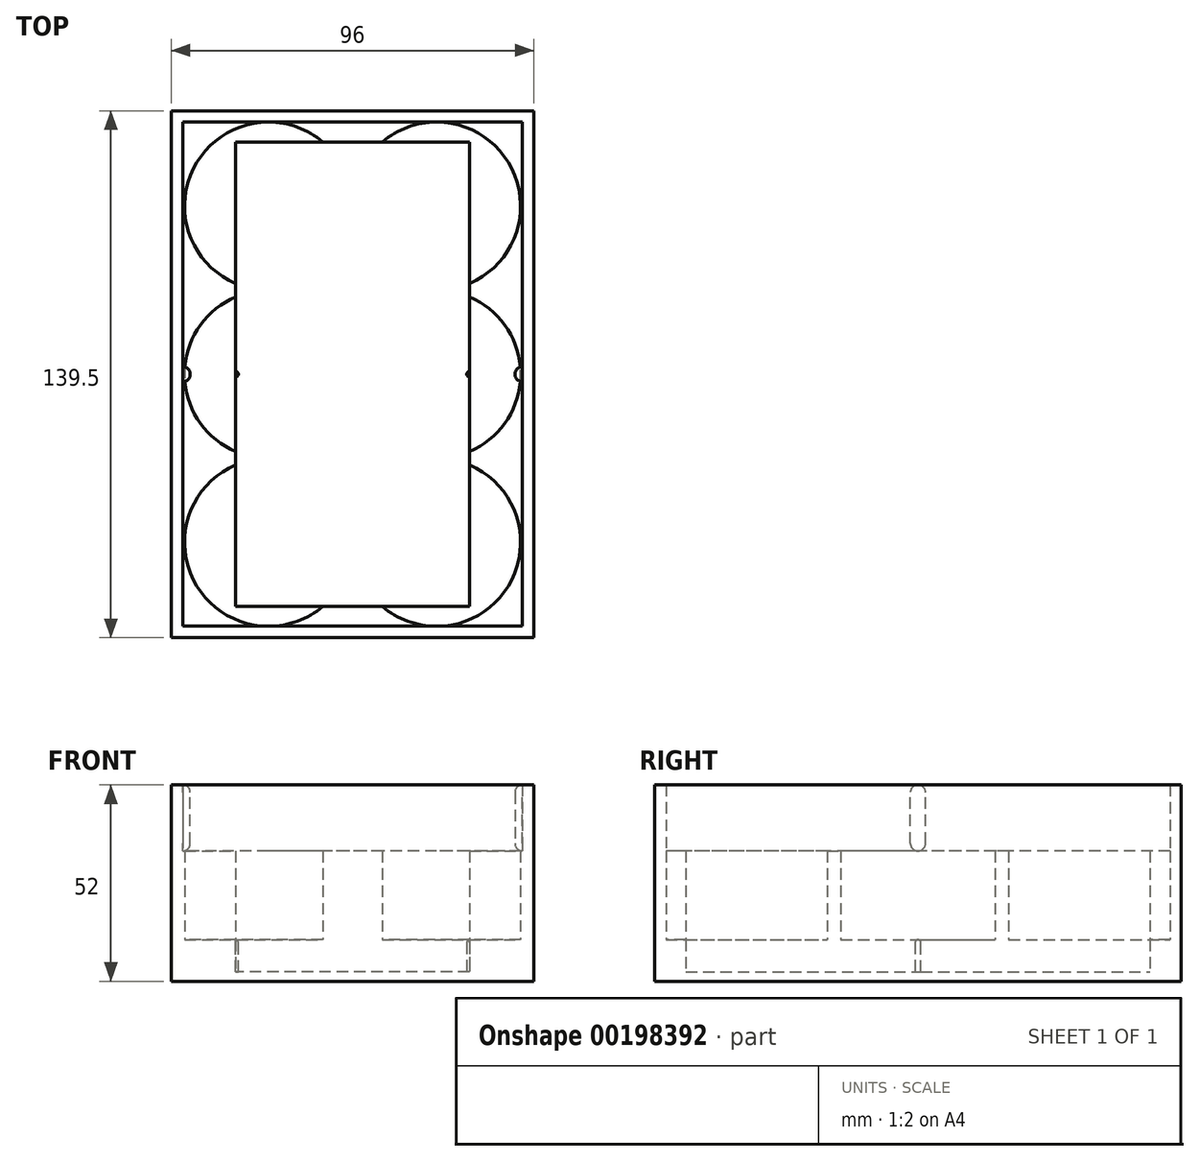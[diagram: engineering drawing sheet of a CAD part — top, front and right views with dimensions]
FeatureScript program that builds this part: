
annotation { "Feature Type Name" : "Feature", "Feature Type Description" : "" }
export const myFeature = defineFeature(function(context is Context, id is Id, definition is map)
    precondition{}
    {
        {
            var Q0;
            Q0=qCreatedBy(makeId("Top.planeOp"),FACE);
            var sketch = newSketch(context, id + "F0", { "sketchPlane" : qUnion([Q0])});
            skLineSegment(sketch, "E0.rect.bottom", {"start": v(47, 68.75) * mm, "end": v(-47, 68.75) * mm});
            skLineSegment(sketch, "E0.rect.top", {"start": v(47, -68.75) * mm, "end": v(-47, -68.75) * mm});
            skLineSegment(sketch, "E0.rect.left", {"start": v(47, 68.75) * mm, "end": v(47, -68.75) * mm});
            skLineSegment(sketch, "E0.rect.right", {"start": v(-47, 68.75) * mm, "end": v(-47, -68.75) * mm});
            skPoint(sketch, "E0.rect.middle", {"position": v(0, 0) * mm});
            skSolve(sketch);
        }
        {
            var Q0;
            Q0=qSketchRegion(id+"F0",true);
            extrude(context, id + "F1", {"entities" : qUnion([Q0]), "depth" : 2.5 * mm});
        }
        {
            var Q0;
            Q0=makeQuery(id+"F1.opExtrude","CAP_FACE",FACE,{"disambiguationData":[OSD([sQuery(id+"F0.wireOp",EDGE,"E0.rect.bottom"),sQuery(id+"F0.wireOp",EDGE,"E0.rect.top"),sQuery(id+"F0.wireOp",EDGE,"E0.rect.left"),sQuery(id+"F0.wireOp",EDGE,"E0.rect.right")])],"isStart":false});
            var sketch = newSketch(context, id + "F2", { "sketchPlane" : qUnion([Q0])});
            skLineSegment(sketch, "E1.rect.bottom", {"start": v(47, 68.75) * mm, "end": v(-47, 68.75) * mm});
            skLineSegment(sketch, "E1.rect.top", {"start": v(47, -68.75) * mm, "end": v(-47, -68.75) * mm});
            skLineSegment(sketch, "E1.rect.left", {"start": v(47, 68.75) * mm, "end": v(47, -68.75) * mm});
            skLineSegment(sketch, "E1.rect.right", {"start": v(-47, 68.75) * mm, "end": v(-47, -68.75) * mm});
            skPoint(sketch, "E1.rect.middle", {"position": v(0, 0) * mm});
            skLineSegment(sketch, "E2.rect.bottom", {"start": v(31, -61.5) * mm, "end": v(-31, -61.5) * mm});
            skLineSegment(sketch, "E2.rect.top", {"start": v(31, 61.5) * mm, "end": v(-31, 61.5) * mm});
            skLineSegment(sketch, "E2.rect.left", {"start": v(31, -61.5) * mm, "end": v(31, 61.5) * mm});
            skLineSegment(sketch, "E2.rect.right", {"start": v(-31, -61.5) * mm, "end": v(-31, 61.5) * mm});
            skSolve(sketch);
        }
        {
            var Q0;
            Q0=qSketchRegion(id+"F2",true);
            extrude(context, id + "F3", {"entities" : qUnion([Q0]), "operationType" : NewBodyOperationType.ADD, "depth" : 8.5 * mm});
        }
        {
            var Q0;
            Q0=makeQuery(id+"F3.opExtrude","CAP_FACE",FACE,{"disambiguationData":[OSD([sQuery(id+"F2.wireOp",EDGE,"E1.rect.bottom"),sQuery(id+"F2.wireOp",EDGE,"E1.rect.top"),sQuery(id+"F2.wireOp",EDGE,"E1.rect.left"),sQuery(id+"F2.wireOp",EDGE,"E1.rect.right"),sQuery(id+"F2.wireOp",EDGE,"E2.rect.bottom"),sQuery(id+"F2.wireOp",EDGE,"E2.rect.top"),sQuery(id+"F2.wireOp",EDGE,"E2.rect.left"),sQuery(id+"F2.wireOp",EDGE,"E2.rect.right")])],"isStart":false});
            var sketch = newSketch(context, id + "F4", { "sketchPlane" : qUnion([Q0])});
            skPoint(sketch, "E3.rect.middle", {"position": v(0, 0) * mm});
            skCircle(sketch, "E4", {"center": v(-22.25, 44.5) * mm, "radius": 22.25 * mm});
            skCircle(sketch, "E5", {"center": v(-22.25, -44.5) * mm, "radius": 22.25 * mm});
            skCircle(sketch, "E6", {"center": v(22.25, -44.5) * mm, "radius": 22.25 * mm});
            skCircle(sketch, "E7", {"center": v(22.25, 0) * mm, "radius": 22.25 * mm});
            skCircle(sketch, "E8", {"center": v(-22.25, 0) * mm, "radius": 22.25 * mm});
            skCircle(sketch, "E9", {"center": v(22.25, 44.5) * mm, "radius": 22.25 * mm});
            skLineSegment(sketch, "E10.rect.bottom", {"start": v(47, -68.75) * mm, "end": v(-47, -68.75) * mm});
            skLineSegment(sketch, "E10.rect.top", {"start": v(47, 68.75) * mm, "end": v(-47, 68.75) * mm});
            skLineSegment(sketch, "E10.rect.left", {"start": v(47, -68.75) * mm, "end": v(47, 68.75) * mm});
            skLineSegment(sketch, "E10.rect.right", {"start": v(-47, -68.75) * mm, "end": v(-47, 68.75) * mm});
            skLineSegment(sketch, "E11", {"start": v(-22.25, 44.5) * mm, "end": v(22.25, 44.5) * mm});
            skLineSegment(sketch, "E12", {"start": v(-22.25, 0) * mm, "end": v(22.25, 0) * mm});
            skLineSegment(sketch, "E13", {"start": v(-22.25, -44.5) * mm, "end": v(22.25, -44.5) * mm});
            skSolve(sketch);
        }
        {
            var Q0;
            Q0=qSketchRegion(id+"F4",true);
            extrude(context, id + "F5", {"entities" : qUnion([Q0]), "operationType" : NewBodyOperationType.ADD, "depth" : 23.5 * mm});
        }
        {
            var Q0;
            {var subQ0=sQuery(id+"F2.wireOp",EDGE,"E2.rect.top");var subQ1=sQuery(id+"F2.wireOp",EDGE,"E2.rect.right");var subQ2=sQuery(id+"F4.wireOp",EDGE,"E4");Q0=makeQuery(id+"F5.boolean.opBoolean","SPLIT",FACE,{"disambiguationData":[TD([makeQuery(id+"F5.opExtrude","SWEPT_FACE",FACE,{"disambiguationData":[OSD([subQ2])]})])],"derivedFrom":makeQuery(id+"F3.opExtrude","CAP_FACE",FACE,{"disambiguationData":[OSD([sQuery(id+"F2.wireOp",EDGE,"E1.rect.bottom"),sQuery(id+"F2.wireOp",EDGE,"E1.rect.top"),sQuery(id+"F2.wireOp",EDGE,"E1.rect.left"),sQuery(id+"F2.wireOp",EDGE,"E1.rect.right"),sQuery(id+"F2.wireOp",EDGE,"E2.rect.bottom"),subQ0,sQuery(id+"F2.wireOp",EDGE,"E2.rect.left"),subQ1])],"isStart":false})});}
            var sketch = newSketch(context, id + "F6", { "sketchPlane" : qUnion([Q0])});
            skLineSegment(sketch, "E14.rect.bottom", {"start": v(-31, 61.5) * mm, "end": v(31, 61.5) * mm});
            skLineSegment(sketch, "E14.rect.top", {"start": v(-31, -61.5) * mm, "end": v(31, -61.5) * mm});
            skLineSegment(sketch, "E14.rect.left", {"start": v(-31, 61.5) * mm, "end": v(-31, -61.5) * mm});
            skLineSegment(sketch, "E14.rect.right", {"start": v(31, 61.5) * mm, "end": v(31, -61.5) * mm});
            skPoint(sketch, "E14.rect.middle", {"position": v(0, 0) * mm});
            skSolve(sketch);
        }
        {
            var Q0;
            Q0=qSketchRegion(id+"F6",true);
            extrude(context, id + "F7", {"entities" : qUnion([Q0]), "operationType" : NewBodyOperationType.REMOVE, "endBound" : BoundingType.THROUGH_ALL, "depth" : 25 * mm});
        }
        {
            var Q0;
            Q0=makeQuery(id+"F5.opExtrude","CAP_FACE",FACE,{"disambiguationData":[OSD([sQuery(id+"F4.wireOp",EDGE,"E4"),sQuery(id+"F4.wireOp",EDGE,"E5"),sQuery(id+"F4.wireOp",EDGE,"E6"),sQuery(id+"F4.wireOp",EDGE,"E7"),sQuery(id+"F4.wireOp",EDGE,"E8"),sQuery(id+"F4.wireOp",EDGE,"E9"),sQuery(id+"F4.wireOp",EDGE,"E10.rect.bottom"),sQuery(id+"F4.wireOp",EDGE,"E10.rect.top"),sQuery(id+"F4.wireOp",EDGE,"E10.rect.left"),sQuery(id+"F4.wireOp",EDGE,"E10.rect.right")])],"isStart":false});
            var sketch = newSketch(context, id + "F8", { "sketchPlane" : qUnion([Q0])});
            skLineSegment(sketch, "E15.rect.bottom", {"start": v(47, 68.75) * mm, "end": v(-47, 68.75) * mm});
            skLineSegment(sketch, "E15.rect.top", {"start": v(47, -68.75) * mm, "end": v(-47, -68.75) * mm});
            skLineSegment(sketch, "E15.rect.left", {"start": v(47, 68.75) * mm, "end": v(47, -68.75) * mm});
            skLineSegment(sketch, "E15.rect.right", {"start": v(-47, 68.75) * mm, "end": v(-47, -68.75) * mm});
            skPoint(sketch, "E15.rect.middle", {"position": v(0, 0) * mm});
            skLineSegment(sketch, "E16.rect.bottom", {"start": v(45, 66.75) * mm, "end": v(-45, 66.75) * mm});
            skLineSegment(sketch, "E16.rect.top", {"start": v(45, -66.75) * mm, "end": v(-45, -66.75) * mm});
            skLineSegment(sketch, "E16.rect.left", {"start": v(45, 66.75) * mm, "end": v(45, -66.75) * mm});
            skLineSegment(sketch, "E16.rect.right", {"start": v(-45, 66.75) * mm, "end": v(-45, -66.75) * mm});
            skSolve(sketch);
        }
        {
            var Q0;
            Q0=qSketchRegion(id+"F8",true);
            extrude(context, id + "F9", {"entities" : qUnion([Q0]), "operationType" : NewBodyOperationType.ADD, "depth" : 17.5 * mm});
        }
        {
            var Q0;
            Q0=makeQuery(id+"F9.opExtrude","SWEPT_FACE",FACE,{"disambiguationData":[OSD([sQuery(id+"F8.wireOp",EDGE,"E16.rect.right")])]});
            var sketch = newSketch(context, id + "F10", { "sketchPlane" : qUnion([Q0])});
            skLineSegment(sketch, "E17", {"start": v(0, 34.5) * mm, "end": v(0, 52) * mm});
            skLineSegment(sketch, "E18", {"start": v(0, 52) * mm, "end": v(0, 50) * mm});
            skLineSegment(sketch, "E19", {"start": v(0, 34.5) * mm, "end": v(0, 36.5) * mm});
            skLineSegment(sketch, "E20", {"start": v(2, 50) * mm, "end": v(2, 36.5) * mm});
            skLineSegment(sketch, "E21", {"start": v(0, 52) * mm, "end": v(0, 34.5) * mm});
            skArc(sketch, "E22", {"start": v(2, 50) * mm, "mid": v(1.41, 51.41) * mm, "end": v(0, 52) * mm});
            skArc(sketch, "E23", {"start": v(0, 34.5) * mm, "mid": v(1.41, 35.09) * mm, "end": v(2, 36.5) * mm});
            skSolve(sketch);
        }
        {
            var Q0;
            Q0=qSketchRegion(id+"F10",true);
            var Q1;
            Q1=sQuery(id+"F10.wireOp",EDGE,"E21");
            revolve(context, id + "F11", {"operationType" : NewBodyOperationType.ADD, "entities" : qUnion([Q0]), "axis" : qUnion([Q1]), "revolveType" : RevolveType.ONE_DIRECTION, "angle" : 180 * degree});
        }
        {
            var Q0;
            Q0=makeQuery(id+"F9.opExtrude","SWEPT_FACE",FACE,{"disambiguationData":[OSD([sQuery(id+"F8.wireOp",EDGE,"E16.rect.left")])]});
            var sketch = newSketch(context, id + "F12", { "sketchPlane" : qUnion([Q0])});
            skLineSegment(sketch, "E24", {"start": v(0, 34.5) * mm, "end": v(0, 52) * mm});
            skLineSegment(sketch, "E25", {"start": v(0, 34.5) * mm, "end": v(0, 36.5) * mm});
            skLineSegment(sketch, "E26", {"start": v(0, 52) * mm, "end": v(0, 50) * mm});
            skLineSegment(sketch, "E27", {"start": v(-2, 36.5) * mm, "end": v(-2, 50) * mm});
            skLineSegment(sketch, "E28", {"start": v(0, 50) * mm, "end": v(-2, 50) * mm});
            skArc(sketch, "E29", {"start": v(0, 52) * mm, "mid": v(-1.41, 51.41) * mm, "end": v(-2, 50) * mm});
            skArc(sketch, "E30", {"start": v(-2, 36.5) * mm, "mid": v(-1.41, 35.09) * mm, "end": v(0, 34.5) * mm});
            skSolve(sketch);
        }
        {
            var Q0;
            Q0=qSketchRegion(id+"F12",true);
            var Q1;
            Q1=sQuery(id+"F12.wireOp",EDGE,"E24");
            revolve(context, id + "F13", {"operationType" : NewBodyOperationType.ADD, "entities" : qUnion([Q0]), "axis" : qUnion([Q1]), "revolveType" : RevolveType.ONE_DIRECTION, "angle" : 180 * degree});
        }
        {
            var Q0;
            Q0=makeQuery(id+"F7.boolean.opBoolean","MERGE",FACE,{"derivedFrom":[makeQuery(id+"F3.opExtrude","SWEPT_FACE",FACE,{"disambiguationData":[OSD([sQuery(id+"F2.wireOp",EDGE,"E2.rect.right")])]}),makeQuery(id+"F7.opExtrude","SWEPT_FACE",FACE,{"disambiguationData":[OSD([sQuery(id+"F6.wireOp",EDGE,"E14.rect.left")])]})]});
            var sketch = newSketch(context, id + "F14", { "sketchPlane" : qUnion([Q0])});
            skLineSegment(sketch, "E31", {"start": v(0, 11) * mm, "end": v(0, 2.5) * mm});
            skLineSegment(sketch, "E32", {"start": v(0, 2.5) * mm, "end": v(0.75, 2.5) * mm});
            skLineSegment(sketch, "E33", {"start": v(0, 11) * mm, "end": v(0, 10.25) * mm});
            skLineSegment(sketch, "E34", {"start": v(0, 10.25) * mm, "end": v(0.75, 10.25) * mm});
            skArc(sketch, "E35", {"start": v(0.75, 10.25) * mm, "mid": v(0.53, 10.78) * mm, "end": v(0, 11) * mm});
            skLineSegment(sketch, "E36", {"start": v(0.75, 10.25) * mm, "end": v(0.75, 2.5) * mm});
            skSolve(sketch);
        }
        {
            var Q0;
            Q0=qSketchRegion(id+"F14",true);
            var Q1;
            Q1=sQuery(id+"F14.wireOp",EDGE,"E31");
            revolve(context, id + "F15", {"operationType" : NewBodyOperationType.ADD, "entities" : qUnion([Q0]), "axis" : qUnion([Q1]), "revolveType" : RevolveType.FULL});
        }
        {
            var Q0;
            Q0=makeQuery(id+"F7.boolean.opBoolean","MERGE",FACE,{"derivedFrom":[makeQuery(id+"F3.opExtrude","SWEPT_FACE",FACE,{"disambiguationData":[OSD([sQuery(id+"F2.wireOp",EDGE,"E2.rect.left")])]}),makeQuery(id+"F7.opExtrude","SWEPT_FACE",FACE,{"disambiguationData":[OSD([sQuery(id+"F6.wireOp",EDGE,"E14.rect.right")])]})]});
            var sketch = newSketch(context, id + "F16", { "sketchPlane" : qUnion([Q0])});
            skLineSegment(sketch, "E37", {"start": v(0, 2.5) * mm, "end": v(0, 11) * mm});
            skLineSegment(sketch, "E38", {"start": v(0, 2.5) * mm, "end": v(-0.75, 2.5) * mm});
            skLineSegment(sketch, "E39", {"start": v(0, 11) * mm, "end": v(0, 10.25) * mm});
            skLineSegment(sketch, "E40", {"start": v(0, 10.25) * mm, "end": v(-0.75, 10.25) * mm});
            skArc(sketch, "E41", {"start": v(0, 11) * mm, "mid": v(-0.53, 10.78) * mm, "end": v(-0.75, 10.25) * mm});
            skLineSegment(sketch, "E42", {"start": v(-0.75, 2.5) * mm, "end": v(-0.75, 10.25) * mm});
            skSolve(sketch);
        }
        {
            var Q0;
            Q0=qSketchRegion(id+"F16",true);
            var Q1;
            Q1=sQuery(id+"F16.wireOp",EDGE,"E37");
            revolve(context, id + "F17", {"operationType" : NewBodyOperationType.ADD, "entities" : qUnion([Q0]), "axis" : qUnion([Q1]), "revolveType" : RevolveType.FULL});
        }
        {
            var Q0;
            Q0=qCreatedBy(makeId("Top.planeOp"),FACE);
            var sketch = newSketch(context, id + "F18", { "sketchPlane" : qUnion([Q0])});
            skLineSegment(sketch, "E43.0", {"start": v(-47, 68.75) * mm, "end": v(-47, -68.75) * mm});
            skLineSegment(sketch, "E44.0", {"start": v(47, 68.75) * mm, "end": v(-47, 68.75) * mm});
            skLineSegment(sketch, "E45.0", {"start": v(47, 68.75) * mm, "end": v(47, -68.75) * mm});
            skLineSegment(sketch, "E46.0", {"start": v(47, -68.75) * mm, "end": v(-47, -68.75) * mm});
            skLineSegment(sketch, "E47.0", {"start": v(50, 71.75) * mm, "end": v(50, -71.75) * mm});
            skLineSegment(sketch, "E47.1", {"start": v(50, 71.75) * mm, "end": v(-50, 71.75) * mm});
            skLineSegment(sketch, "E47.2", {"start": v(-50, 71.75) * mm, "end": v(-50, -71.75) * mm});
            skLineSegment(sketch, "E47.3", {"start": v(50, -71.75) * mm, "end": v(-50, -71.75) * mm});
            skSolve(sketch);
        }
        {
            var Q0;
            Q0=makeQuery(id+"F9.boolean.opBoolean","MERGE",FACE,{"derivedFrom":[makeQuery(id+"F5.boolean.opBoolean","MERGE",FACE,{"derivedFrom":[makeQuery(id+"F3.boolean.opBoolean","MERGE",FACE,{"derivedFrom":[makeQuery(id+"F1.opExtrude","SWEPT_FACE",FACE,{"disambiguationData":[OSD([sQuery(id+"F0.wireOp",EDGE,"E0.rect.left")])]}),makeQuery(id+"F3.opExtrude","SWEPT_FACE",FACE,{"disambiguationData":[OSD([sQuery(id+"F2.wireOp",EDGE,"E1.rect.left")])]})]}),makeQuery(id+"F5.opExtrude","SWEPT_FACE",FACE,{"disambiguationData":[OSD([sQuery(id+"F4.wireOp",EDGE,"E10.rect.left")])]})]}),makeQuery(id+"F9.opExtrude","SWEPT_FACE",FACE,{"disambiguationData":[OSD([sQuery(id+"F8.wireOp",EDGE,"E15.rect.left")])]})]});
            extrude(context, id + "F19", {"entities" : qUnion([Q0]), "operationType" : NewBodyOperationType.ADD, "depth" : 1 * mm});
        }
        {
            var Q0;
            Q0=makeQuery(id+"F9.boolean.opBoolean","MERGE",FACE,{"derivedFrom":[makeQuery(id+"F5.boolean.opBoolean","MERGE",FACE,{"derivedFrom":[makeQuery(id+"F3.boolean.opBoolean","MERGE",FACE,{"derivedFrom":[makeQuery(id+"F1.opExtrude","SWEPT_FACE",FACE,{"disambiguationData":[OSD([sQuery(id+"F0.wireOp",EDGE,"E0.rect.right")])]}),makeQuery(id+"F3.opExtrude","SWEPT_FACE",FACE,{"disambiguationData":[OSD([sQuery(id+"F2.wireOp",EDGE,"E1.rect.right")])]})]}),makeQuery(id+"F5.opExtrude","SWEPT_FACE",FACE,{"disambiguationData":[OSD([sQuery(id+"F4.wireOp",EDGE,"E10.rect.right")])]})]}),makeQuery(id+"F9.opExtrude","SWEPT_FACE",FACE,{"disambiguationData":[OSD([sQuery(id+"F8.wireOp",EDGE,"E15.rect.right")])]})]});
            extrude(context, id + "F20", {"entities" : qUnion([Q0]), "operationType" : NewBodyOperationType.ADD, "depth" : 1 * mm});
        }
        {
            var Q0;
            {var subQ0=sQuery(id+"F8.wireOp",EDGE,"E15.rect.top");var subQ1=sQuery(id+"F4.wireOp",EDGE,"E10.rect.bottom");var subQ2=sQuery(id+"F2.wireOp",EDGE,"E1.rect.top");var subQ3=sQuery(id+"F0.wireOp",EDGE,"E0.rect.top");Q0=makeQuery(id+"F20.boolean.opBoolean","MERGE",FACE,{"derivedFrom":[makeQuery(id+"F19.boolean.opBoolean","MERGE",FACE,{"derivedFrom":[makeQuery(id+"F9.boolean.opBoolean","MERGE",FACE,{"derivedFrom":[makeQuery(id+"F5.boolean.opBoolean","MERGE",FACE,{"derivedFrom":[makeQuery(id+"F3.boolean.opBoolean","MERGE",FACE,{"derivedFrom":[makeQuery(id+"F1.opExtrude","SWEPT_FACE",FACE,{"disambiguationData":[OSD([subQ3])]}),makeQuery(id+"F3.opExtrude","SWEPT_FACE",FACE,{"disambiguationData":[OSD([subQ2])]})]}),makeQuery(id+"F5.opExtrude","SWEPT_FACE",FACE,{"disambiguationData":[OSD([subQ1])]})]}),makeQuery(id+"F9.opExtrude","SWEPT_FACE",FACE,{"disambiguationData":[OSD([subQ0])]})]}),makeQuery(id+"F19.opExtrude","SWEPT_FACE",FACE,{"disambiguationData":[OSD([subQ3,sQuery(id+"F0.wireOp",EDGE,"E0.rect.left"),subQ2,sQuery(id+"F2.wireOp",EDGE,"E1.rect.left"),subQ1,sQuery(id+"F4.wireOp",EDGE,"E10.rect.left"),subQ0,sQuery(id+"F8.wireOp",EDGE,"E15.rect.left")])]})]}),makeQuery(id+"F20.opExtrude","SWEPT_FACE",FACE,{"disambiguationData":[OSD([subQ3,sQuery(id+"F0.wireOp",EDGE,"E0.rect.right"),subQ2,sQuery(id+"F2.wireOp",EDGE,"E1.rect.right"),subQ1,sQuery(id+"F4.wireOp",EDGE,"E10.rect.right"),subQ0,sQuery(id+"F8.wireOp",EDGE,"E15.rect.right")])]})]});}
            extrude(context, id + "F21", {"entities" : qUnion([Q0]), "operationType" : NewBodyOperationType.ADD, "depth" : 1 * mm});
        }
        {
            var Q0;
            {var subQ0=sQuery(id+"F8.wireOp",EDGE,"E15.rect.bottom");var subQ1=sQuery(id+"F4.wireOp",EDGE,"E10.rect.top");var subQ2=sQuery(id+"F2.wireOp",EDGE,"E1.rect.bottom");var subQ3=sQuery(id+"F0.wireOp",EDGE,"E0.rect.bottom");Q0=makeQuery(id+"F20.boolean.opBoolean","MERGE",FACE,{"derivedFrom":[makeQuery(id+"F19.boolean.opBoolean","MERGE",FACE,{"derivedFrom":[makeQuery(id+"F9.boolean.opBoolean","MERGE",FACE,{"derivedFrom":[makeQuery(id+"F5.boolean.opBoolean","MERGE",FACE,{"derivedFrom":[makeQuery(id+"F3.boolean.opBoolean","MERGE",FACE,{"derivedFrom":[makeQuery(id+"F1.opExtrude","SWEPT_FACE",FACE,{"disambiguationData":[OSD([subQ3])]}),makeQuery(id+"F3.opExtrude","SWEPT_FACE",FACE,{"disambiguationData":[OSD([subQ2])]})]}),makeQuery(id+"F5.opExtrude","SWEPT_FACE",FACE,{"disambiguationData":[OSD([subQ1])]})]}),makeQuery(id+"F9.opExtrude","SWEPT_FACE",FACE,{"disambiguationData":[OSD([subQ0])]})]}),makeQuery(id+"F19.opExtrude","SWEPT_FACE",FACE,{"disambiguationData":[OSD([subQ3,sQuery(id+"F0.wireOp",EDGE,"E0.rect.left"),subQ2,sQuery(id+"F2.wireOp",EDGE,"E1.rect.left"),subQ1,sQuery(id+"F4.wireOp",EDGE,"E10.rect.left"),subQ0,sQuery(id+"F8.wireOp",EDGE,"E15.rect.left")])]})]}),makeQuery(id+"F20.opExtrude","SWEPT_FACE",FACE,{"disambiguationData":[OSD([subQ3,sQuery(id+"F0.wireOp",EDGE,"E0.rect.right"),subQ2,sQuery(id+"F2.wireOp",EDGE,"E1.rect.right"),subQ1,sQuery(id+"F4.wireOp",EDGE,"E10.rect.right"),subQ0,sQuery(id+"F8.wireOp",EDGE,"E15.rect.right")])]})]});}
            extrude(context, id + "F22", {"entities" : qUnion([Q0]), "operationType" : NewBodyOperationType.ADD, "depth" : 1 * mm});
        }
    });
